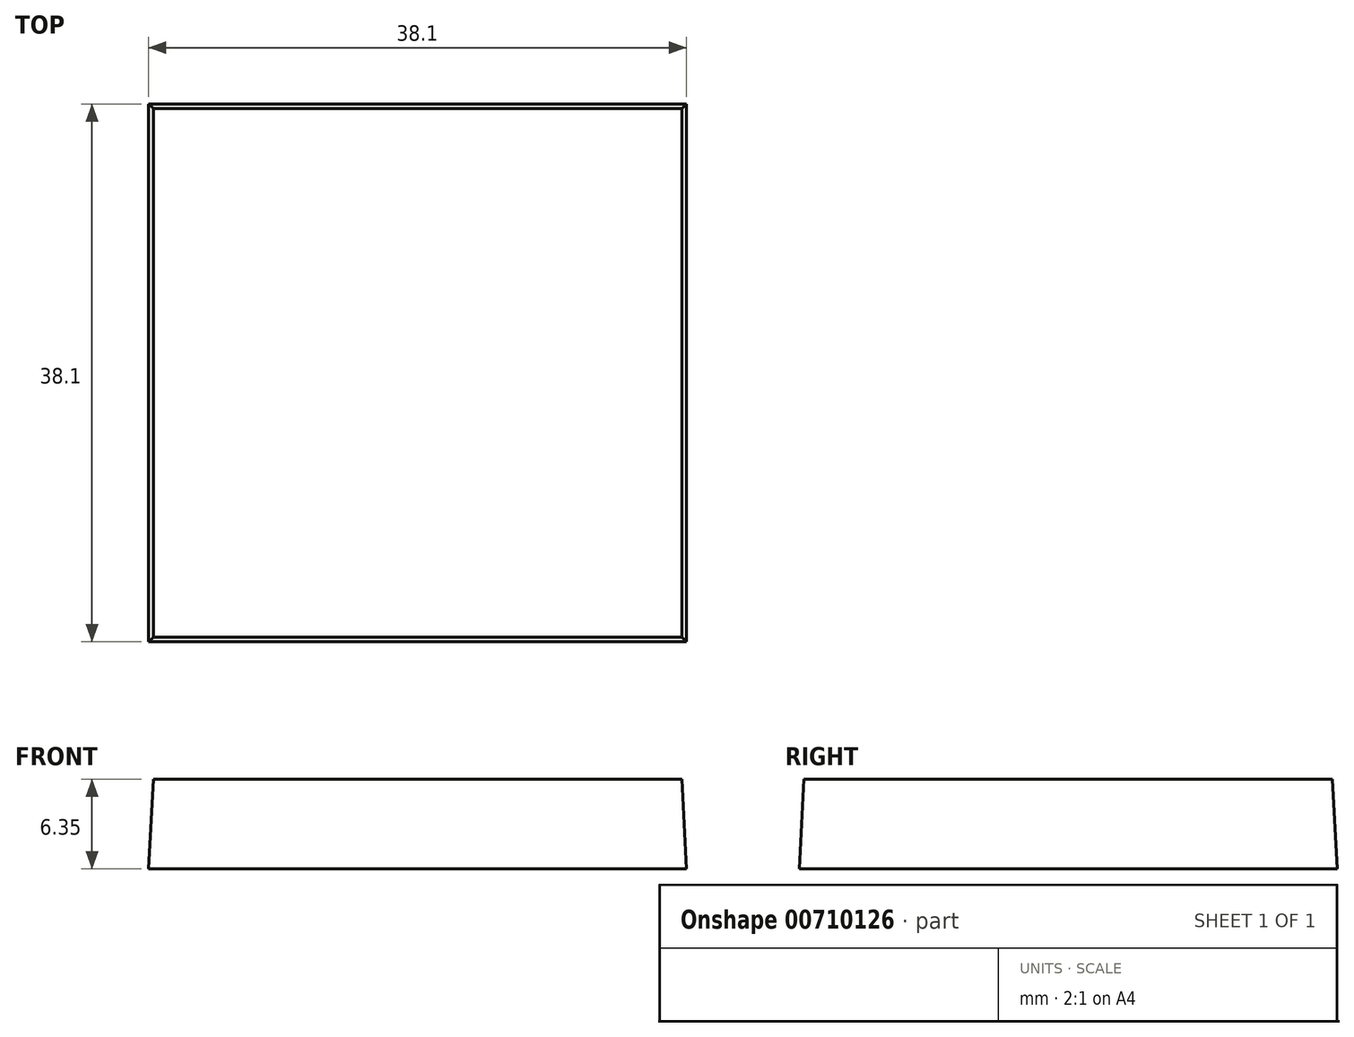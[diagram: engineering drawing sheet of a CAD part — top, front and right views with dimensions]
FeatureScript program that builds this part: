
annotation { "Feature Type Name" : "Feature", "Feature Type Description" : "" }
export const myFeature = defineFeature(function(context is Context, id is Id, definition is map)
    precondition{}
    {
        {
            var Q0;
            Q0=qCreatedBy(makeId("Top.planeOp"),FACE);
            var sketch = newSketch(context, id + "F0", { "sketchPlane" : qUnion([Q0])});
            skLineSegment(sketch, "E0.bottom", {"start": v(19.05, -19.05) * mm, "end": v(-19.05, -19.05) * mm});
            skLineSegment(sketch, "E0.top", {"start": v(19.05, 19.05) * mm, "end": v(-19.05, 19.05) * mm});
            skLineSegment(sketch, "E0.left", {"start": v(19.05, -19.05) * mm, "end": v(19.05, 19.05) * mm});
            skLineSegment(sketch, "E0.right", {"start": v(-19.05, -19.05) * mm, "end": v(-19.05, 19.05) * mm});
            skPoint(sketch, "E0.middle", {"position": v(0, 0) * mm});
            skSolve(sketch);
        }
        {
            var Q0;
            Q0 = qSketchRegion(id + "F0", true);
            extrude(context, id + "F1", {"entities" : qUnion([Q0]), "depth" : 6.35 * mm, "offsetDistance" : 25.4 * mm, "hasDraft" : true, "draftAngle" : 3 * degree, "draftPullDirection" : true});
        }
    });
